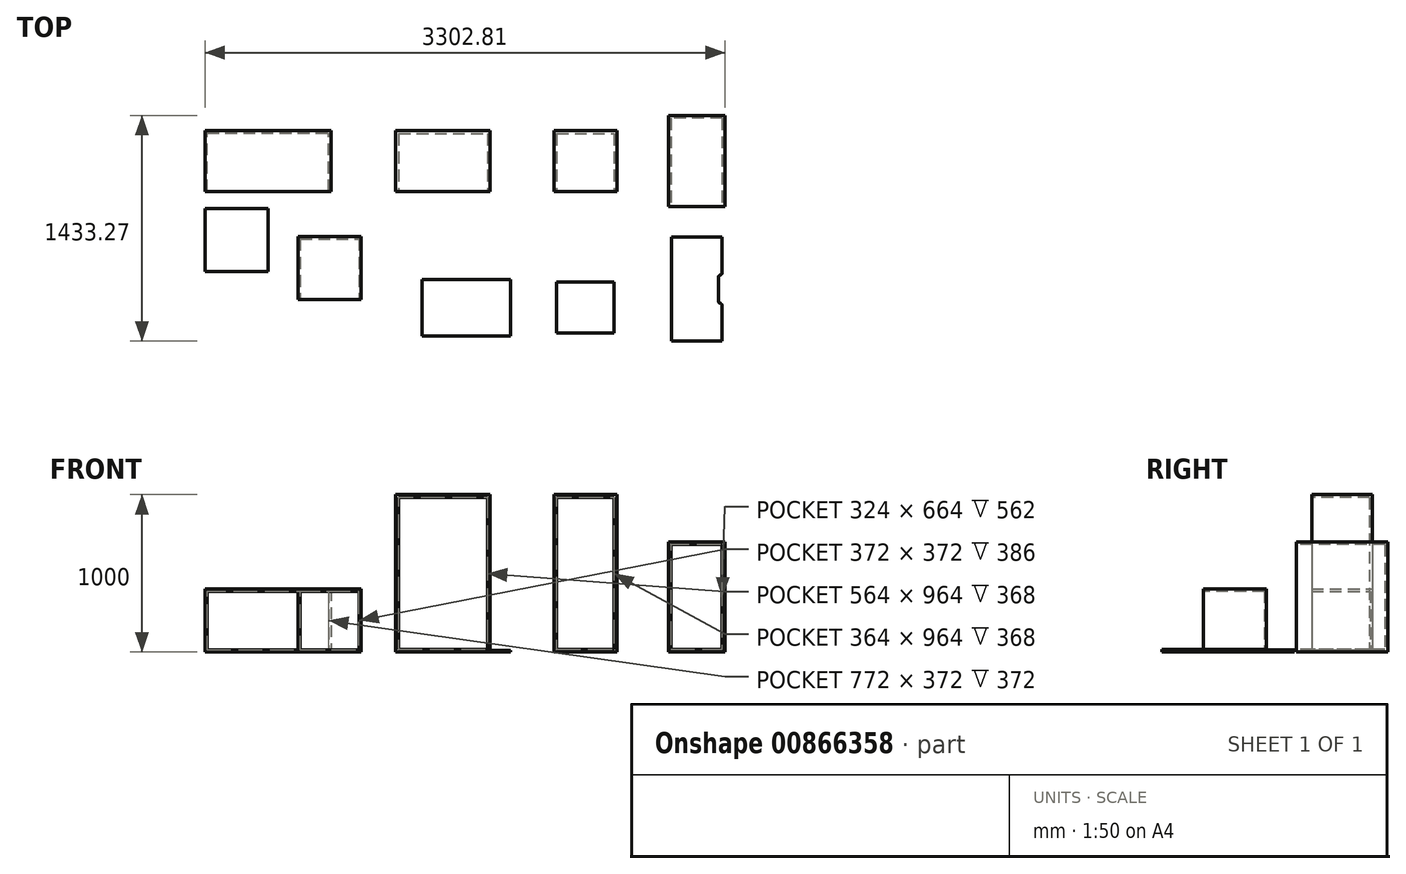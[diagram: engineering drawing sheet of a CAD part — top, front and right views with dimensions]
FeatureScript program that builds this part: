
annotation { "Feature Type Name" : "Feature", "Feature Type Description" : "" }
export const myFeature = defineFeature(function(context is Context, id is Id, definition is map)
    precondition{}
    {
        {
            var Q0;
            Q0=qCreatedBy(makeId("Top.planeOp"),FACE);
            var sketch = newSketch(context, id + "F0", { "sketchPlane" : qUnion([Q0])});
            skLineSegment(sketch, "E0.bottom", {"start": v(-221.94, -79.31) * mm, "end": v(378.06, -79.31) * mm});
            skLineSegment(sketch, "E0.top", {"start": v(-221.94, -465.31) * mm, "end": v(378.06, -465.31) * mm});
            skLineSegment(sketch, "E0.left", {"start": v(-221.94, -79.31) * mm, "end": v(-221.94, -465.31) * mm});
            skLineSegment(sketch, "E0.right", {"start": v(378.06, -79.31) * mm, "end": v(378.06, -465.31) * mm});
            skPoint(sketch, "E0.middle", {"position": v(78.06, -272.31) * mm});
            skLineSegment(sketch, "E1.bottom", {"start": v(508, -1023.45) * mm, "end": v(-56, -1023.45) * mm});
            skLineSegment(sketch, "E1.top", {"start": v(508, -1383.45) * mm, "end": v(-56, -1383.45) * mm});
            skLineSegment(sketch, "E1.left", {"start": v(508, -1023.45) * mm, "end": v(508, -1383.45) * mm});
            skLineSegment(sketch, "E1.right", {"start": v(-56, -1023.45) * mm, "end": v(-56, -1383.45) * mm});
            skPoint(sketch, "E1.middle", {"position": v(226, -1203.45) * mm});
            skLineSegment(sketch, "E2.bottom", {"start": v(782.13, -79.31) * mm, "end": v(1182.13, -79.31) * mm});
            skLineSegment(sketch, "E2.top", {"start": v(782.13, -465.31) * mm, "end": v(1182.13, -465.31) * mm});
            skLineSegment(sketch, "E2.left", {"start": v(782.13, -79.31) * mm, "end": v(782.13, -465.31) * mm});
            skLineSegment(sketch, "E2.right", {"start": v(1182.13, -79.31) * mm, "end": v(1182.13, -465.31) * mm});
            skPoint(sketch, "E2.middle", {"position": v(982.13, -272.31) * mm});
            skPoint(sketch, "E2.middle.positionSnap0", {"position": v(378.06, -272.31) * mm});
            skPoint(sketch, "E2.centerSnap0", {"position": v(378.06, -272.31) * mm});
            skLineSegment(sketch, "E3.bottom", {"start": v(1182.13, -1023.45) * mm, "end": v(782.13, -1023.45) * mm, "construction": true});
            skLineSegment(sketch, "E3.top", {"start": v(1182.13, -1383.45) * mm, "end": v(782.13, -1383.45) * mm, "construction": true});
            skLineSegment(sketch, "E3.left", {"start": v(1182.13, -1023.45) * mm, "end": v(1182.13, -1383.45) * mm, "construction": true});
            skLineSegment(sketch, "E3.right", {"start": v(782.13, -1023.45) * mm, "end": v(782.13, -1383.45) * mm, "construction": true});
            skPoint(sketch, "E3.middle", {"position": v(982.13, -1203.45) * mm});
            skLineSegment(sketch, "E4.0", {"start": v(800.13, -1041.45) * mm, "end": v(800.13, -1365.45) * mm});
            skLineSegment(sketch, "E4.1", {"start": v(1164.13, -1041.45) * mm, "end": v(800.13, -1041.45) * mm});
            skLineSegment(sketch, "E4.2", {"start": v(1164.13, -1041.45) * mm, "end": v(1164.13, -1365.45) * mm});
            skLineSegment(sketch, "E4.3", {"start": v(1164.13, -1365.45) * mm, "end": v(800.13, -1365.45) * mm});
            skLineSegment(sketch, "E5.bottom", {"start": v(1868.85, 17.69) * mm, "end": v(1508.85, 17.69) * mm});
            skLineSegment(sketch, "E5.top", {"start": v(1868.85, -562.31) * mm, "end": v(1508.85, -562.31) * mm});
            skLineSegment(sketch, "E5.left", {"start": v(1868.85, 17.69) * mm, "end": v(1868.85, -562.31) * mm});
            skLineSegment(sketch, "E5.right", {"start": v(1508.85, 17.69) * mm, "end": v(1508.85, -562.31) * mm});
            skPoint(sketch, "E5.middle", {"position": v(1688.85, -272.31) * mm});
            skPoint(sketch, "E5.middle.positionSnap0", {"position": v(1182.13, -272.31) * mm});
            skPoint(sketch, "E5.centerSnap0", {"position": v(1182.13, -272.31) * mm});
            skLineSegment(sketch, "E6.bottom", {"start": v(1848.85, -755.58) * mm, "end": v(1528.85, -755.58) * mm});
            skLineSegment(sketch, "E6.top", {"start": v(1848.85, -1415.58) * mm, "end": v(1528.85, -1415.58) * mm});
            skLineSegment(sketch, "E6.left", {"start": v(1848.85, -755.58) * mm, "end": v(1848.85, -986) * mm});
            skLineSegment(sketch, "E6.right", {"start": v(1528.85, -755.58) * mm, "end": v(1528.85, -1415.58) * mm});
            skPoint(sketch, "E6.middle", {"position": v(1688.85, -1085.58) * mm});
            skLineSegment(sketch, "E7.bottom", {"start": v(1838.85, -996) * mm, "end": v(1838.85, -996) * mm});
            skLineSegment(sketch, "E7.top", {"start": v(1838.85, -1175.15) * mm, "end": v(1838.85, -1175.15) * mm});
            skLineSegment(sketch, "E7.left", {"start": v(1828.85, -1006) * mm, "end": v(1828.85, -1165.15) * mm});
            skPoint(sketch, "E7.middle", {"position": v(1848.85, -1085.58) * mm});
            skLineSegment(sketch, "E8.trimOffspring", {"start": v(1848.85, -1185.15) * mm, "end": v(1848.85, -1415.58) * mm});
            skPoint(sketch, "E9.visualSharp", {"position": v(1828.85, -996) * mm});
            skArc(sketch, "E9.filletArc", {"start": v(1838.85, -996) * mm, "mid": v(1831.78, -998.93) * mm, "end": v(1828.85, -1006) * mm});
            skPoint(sketch, "E10.visualSharp", {"position": v(1828.85, -1175.15) * mm});
            skArc(sketch, "E10.filletArc", {"start": v(1828.85, -1165.15) * mm, "mid": v(1831.78, -1172.22) * mm, "end": v(1838.85, -1175.15) * mm});
            skPoint(sketch, "E11.visualSharp", {"position": v(1848.85, -1175.15) * mm});
            skArc(sketch, "E11.filletArc", {"start": v(1848.85, -1185.15) * mm, "mid": v(1845.92, -1178.08) * mm, "end": v(1838.85, -1175.15) * mm});
            skPoint(sketch, "E12.visualSharp", {"position": v(1848.85, -996) * mm});
            skArc(sketch, "E12.filletArc", {"start": v(1838.85, -996) * mm, "mid": v(1845.92, -993.08) * mm, "end": v(1848.85, -986) * mm});
            skLineSegment(sketch, "E13.bottom", {"start": v(-1433.96, -465.31) * mm, "end": v(-633.96, -465.31) * mm});
            skLineSegment(sketch, "E13.top", {"start": v(-1433.96, -79.31) * mm, "end": v(-633.96, -79.31) * mm});
            skLineSegment(sketch, "E13.left", {"start": v(-1433.96, -465.31) * mm, "end": v(-1433.96, -79.31) * mm});
            skLineSegment(sketch, "E13.right", {"start": v(-633.96, -465.31) * mm, "end": v(-633.96, -79.31) * mm});
            skPoint(sketch, "E13.middle", {"position": v(-1033.96, -272.31) * mm});
            skPoint(sketch, "E13.middle.positionSnap0", {"position": v(-221.94, -272.31) * mm});
            skPoint(sketch, "E13.centerSnap0", {"position": v(-221.94, -272.31) * mm});
            skLineSegment(sketch, "E14.bottom", {"start": v(-1433.96, -574.68) * mm, "end": v(-1033.96, -574.68) * mm});
            skLineSegment(sketch, "E14.top", {"start": v(-1433.96, -974.68) * mm, "end": v(-1033.96, -974.68) * mm});
            skLineSegment(sketch, "E14.left", {"start": v(-1433.96, -574.68) * mm, "end": v(-1433.96, -974.68) * mm});
            skLineSegment(sketch, "E14.right", {"start": v(-1033.96, -574.68) * mm, "end": v(-1033.96, -974.68) * mm});
            skLineSegment(sketch, "E15.bottom", {"start": v(-842.59, -752.47) * mm, "end": v(-442.59, -752.47) * mm});
            skLineSegment(sketch, "E15.top", {"start": v(-842.59, -1152.47) * mm, "end": v(-442.59, -1152.47) * mm});
            skLineSegment(sketch, "E15.left", {"start": v(-842.59, -752.47) * mm, "end": v(-842.59, -1152.47) * mm});
            skLineSegment(sketch, "E15.right", {"start": v(-442.59, -752.47) * mm, "end": v(-442.59, -1152.47) * mm});
            skSolve(sketch);
        }
        {
            var Q0;
            Q0=makeQuery(id+"F0.imprint","IMPRINT",FACE,{"disambiguationData":[TD([[makeQuery(id+"F0.imprint","IMPRINT",EDGE,{"derivedFrom":sQuery(id+"F0.wireOp",EDGE,"E0.bottom")}),-1.0]])]});
            var Q1;
            Q1=makeQuery(id+"F0.imprint","IMPRINT",FACE,{"disambiguationData":[TD([[makeQuery(id+"F0.imprint","IMPRINT",EDGE,{"derivedFrom":sQuery(id+"F0.wireOp",EDGE,"E2.bottom")}),-1.0]])]});
            extrude(context, id + "F1", {"entities" : qUnion([Q0, Q1]), "depth" : 1000 * mm, "offsetDistance" : 25 * mm});
        }
        {
            var Q0;
            Q0=makeQuery(id+"F1.opExtrude","SWEPT_FACE",FACE,{"disambiguationData":[OSD([sQuery(id+"F0.wireOp",EDGE,"E0.top")])]});
            var Q1;
            Q1=makeQuery(id+"F1.opExtrude","SWEPT_FACE",FACE,{"disambiguationData":[OSD([sQuery(id+"F0.wireOp",EDGE,"E2.top")])]});
            shell(context, id + "F2", {"entities" : qUnion([Q0, Q1]), "thickness" : 18 * mm});
        }
        {
            var Q0;
            Q0=makeQuery(id+"F0.imprint","IMPRINT",FACE,{"disambiguationData":[TD([[makeQuery(id+"F0.imprint","IMPRINT",EDGE,{"derivedFrom":sQuery(id+"F0.wireOp",EDGE,"E1.bottom")}),1.0]])]});
            var Q1;
            Q1=makeQuery(id+"F0.imprint","IMPRINT",FACE,{"disambiguationData":[TD([[makeQuery(id+"F0.imprint","IMPRINT",EDGE,{"derivedFrom":sQuery(id+"F0.wireOp",EDGE,"E4.0")}),1.0]])]});
            extrude(context, id + "F3", {"entities" : qUnion([Q0, Q1]), "depth" : 10 * mm, "offsetDistance" : 25 * mm});
        }
        {
            var Q0;
            Q0=makeQuery(id+"F0.imprint","IMPRINT",FACE,{"disambiguationData":[TD([[makeQuery(id+"F0.imprint","IMPRINT",EDGE,{"derivedFrom":sQuery(id+"F0.wireOp",EDGE,"E5.bottom")}),1.0]])]});
            extrude(context, id + "F4", {"entities" : qUnion([Q0]), "depth" : 700 * mm, "offsetDistance" : 25 * mm});
        }
        {
            var Q0;
            Q0=makeQuery(id+"F4.opExtrude","SWEPT_FACE",FACE,{"disambiguationData":[OSD([sQuery(id+"F0.wireOp",EDGE,"E5.top")])]});
            shell(context, id + "F5", {"entities" : qUnion([Q0]), "thickness" : 18 * mm});
        }
        {
            var Q0;
            Q0=makeQuery(id+"F0.imprint","IMPRINT",FACE,{"disambiguationData":[TD([[makeQuery(id+"F0.imprint","IMPRINT",EDGE,{"derivedFrom":sQuery(id+"F0.wireOp",EDGE,"E6.bottom")}),1.0]])]});
            extrude(context, id + "F6", {"entities" : qUnion([Q0]), "depth" : 18 * mm, "offsetDistance" : 25 * mm});
        }
        {
            var Q0;
            Q0=makeQuery(id+"F0.imprint","IMPRINT",FACE,{"disambiguationData":[TD([[makeQuery(id+"F0.imprint","IMPRINT",EDGE,{"derivedFrom":sQuery(id+"F0.wireOp",EDGE,"E14.bottom")}),-1.0]])]});
            extrude(context, id + "F7", {"entities" : qUnion([Q0]), "depth" : 14 * mm, "offsetDistance" : 25 * mm});
        }
        {
            var Q0;
            Q0=makeQuery(id+"F0.imprint","IMPRINT",FACE,{"disambiguationData":[TD([[makeQuery(id+"F0.imprint","IMPRINT",EDGE,{"derivedFrom":sQuery(id+"F0.wireOp",EDGE,"E13.bottom")}),1.0]])]});
            var Q1;
            Q1=makeQuery(id+"F0.imprint","IMPRINT",FACE,{"disambiguationData":[TD([[makeQuery(id+"F0.imprint","IMPRINT",EDGE,{"derivedFrom":sQuery(id+"F0.wireOp",EDGE,"E15.bottom")}),-1.0]])]});
            extrude(context, id + "F8", {"entities" : qUnion([Q0, Q1]), "depth" : 400 * mm, "offsetDistance" : 25 * mm});
        }
        {
            var Q0;
            Q0=makeQuery(id+"F8.opExtrude","SWEPT_FACE",FACE,{"disambiguationData":[OSD([sQuery(id+"F0.wireOp",EDGE,"E13.bottom")])]});
            var Q1;
            Q1=makeQuery(id+"F8.opExtrude","SWEPT_FACE",FACE,{"disambiguationData":[OSD([sQuery(id+"F0.wireOp",EDGE,"E15.top")])]});
            shell(context, id + "F9", {"entities" : qUnion([Q0, Q1]), "thickness" : 14 * mm});
        }
    });
